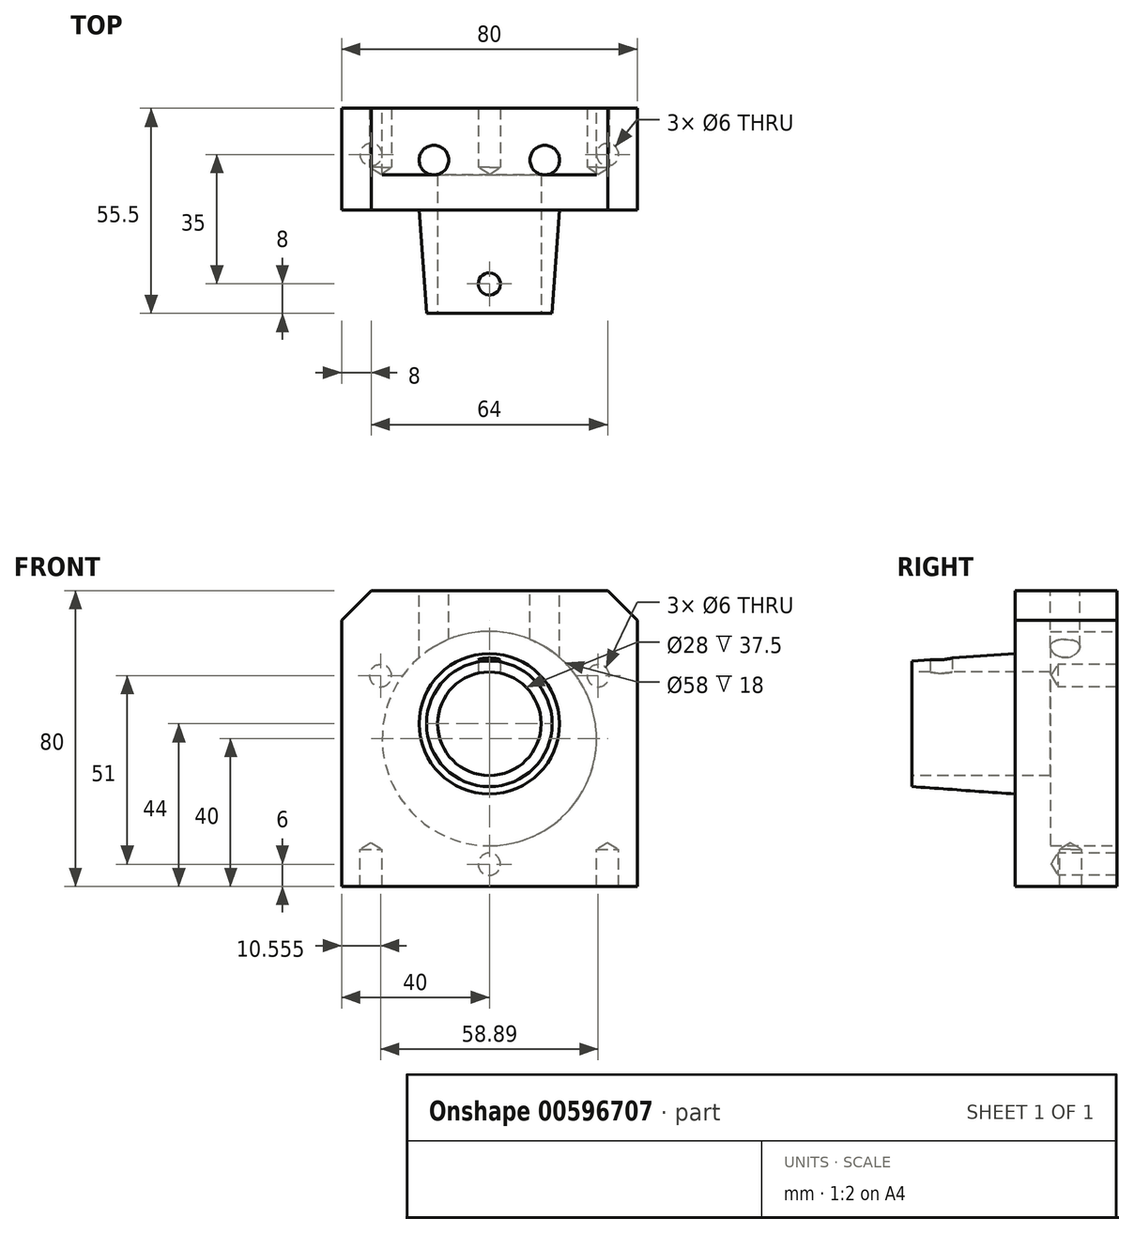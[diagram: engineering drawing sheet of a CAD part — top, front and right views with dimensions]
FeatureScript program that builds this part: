
annotation { "Feature Type Name" : "Feature", "Feature Type Description" : "" }
export const myFeature = defineFeature(function(context is Context, id is Id, definition is map)
    precondition{}
    {
        {
            var Q0;
            Q0=qCreatedBy(makeId("Front.planeOp"),FACE);
            var sketch = newSketch(context, id + "F0", { "sketchPlane" : qUnion([Q0])});
            skLineSegment(sketch, "E0.bottom", {"start": v(-40, 40) * mm, "end": v(40, 40) * mm});
            skLineSegment(sketch, "E0.top", {"start": v(-40, -40) * mm, "end": v(40, -40) * mm});
            skLineSegment(sketch, "E0.left", {"start": v(-40, 40) * mm, "end": v(-40, -40) * mm});
            skLineSegment(sketch, "E0.right", {"start": v(40, 40) * mm, "end": v(40, -40) * mm});
            skCircle(sketch, "E1", {"center": v(0, 0) * mm, "radius": 29 * mm});
            skCircle(sketch, "E2", {"center": v(0, -34) * mm, "radius": 3 * mm});
            skCircle(sketch, "E3.1.0", {"center": v(29.44, 17) * mm, "radius": 3 * mm});
            skCircle(sketch, "E3.2.0", {"center": v(-29.44, 17) * mm, "radius": 3 * mm});
            skSolve(sketch);
        }
        {
            var Q0;
            Q0 = qSketchRegion(id + "F0", true);
            var Q1;
            Q1=makeQuery(id+"F0.imprint","IMPRINT",FACE,{"disambiguationData":[TD([[makeQuery(id+"F0.imprint","IMPRINT",EDGE,{"derivedFrom":sQuery(id+"F0.wireOp",EDGE,"E3.1.0")}),1.0]])]});
            var Q2;
            Q2=makeQuery(id+"F0.imprint","IMPRINT",FACE,{"disambiguationData":[TD([[makeQuery(id+"F0.imprint","IMPRINT",EDGE,{"derivedFrom":sQuery(id+"F0.wireOp",EDGE,"E3.2.0")}),1.0]])]});
            var Q3;
            Q3=makeQuery(id+"F0.imprint","IMPRINT",FACE,{"disambiguationData":[TD([[makeQuery(id+"F0.imprint","IMPRINT",EDGE,{"derivedFrom":sQuery(id+"F0.wireOp",EDGE,"E2")}),1.0]])]});
            var Q4;
            Q4=makeQuery(id+"F0.imprint","IMPRINT",FACE,{"disambiguationData":[TD([[makeQuery(id+"F0.imprint","IMPRINT",EDGE,{"derivedFrom":sQuery(id+"F0.wireOp",EDGE,"E1")}),1.0]])]});
            extrude(context, id + "F1", {"entities" : qUnion([Q0, Q1, Q2, Q3, Q4]), "depth" : 27.5 * mm, "offsetDistance" : 25 * mm});
        }
        {
            var Q0;
            Q0=makeQuery(id+"F1.opExtrude","SWEPT_EDGE",EDGE,{"disambiguationData":[OSD([sQuery(id+"F0.wireOp",EDGE,"E0.bottom"),sQuery(id+"F0.wireOp",EDGE,"E0.right")])]});
            var Q1;
            Q1=makeQuery(id+"F1.opExtrude","SWEPT_EDGE",EDGE,{"disambiguationData":[OSD([sQuery(id+"F0.wireOp",EDGE,"E0.bottom"),sQuery(id+"F0.wireOp",EDGE,"E0.left")])]});
            chamfer(context, id + "F2", {"entities" : qUnion([Q0, Q1]), "width" : 8 * mm, "tangentPropagation" : true});
        }
        {
            var Q0;
            Q0=makeQuery(id+"F1.opExtrude","CAP_FACE",FACE,{"disambiguationData":[OSD([sQuery(id+"F0.wireOp",EDGE,"E0.bottom"),sQuery(id+"F0.wireOp",EDGE,"E0.top"),sQuery(id+"F0.wireOp",EDGE,"E0.left"),sQuery(id+"F0.wireOp",EDGE,"E0.right")])],"isStart":false});
            cPlane(context, id + "F3", {"entities" : qUnion([Q0]), "cplaneType" : CPlaneType.OFFSET, "offset" : 0 * mm, "width" : 150 * mm, "height" : 150 * mm});
        }
        {
            var Q0;
            Q0=qCreatedBy(id+"F3.planeOp",FACE);
            var sketch = newSketch(context, id + "F4", { "sketchPlane" : qUnion([Q0])});
            skPoint(sketch, "E4", {"position": v(0, 4) * mm});
            skSolve(sketch);
        }
        {
            var Q0;
            Q0=qCreatedBy(makeId("Top.planeOp"),FACE);
            var Q1;
            Q1=sQuery(id+"F4.wireOp",VERTEX,"E4");
            cPlane(context, id + "F5", {"entities" : qUnion([Q0, Q1]), "cplaneType" : CPlaneType.PLANE_POINT, "offset" : 25 * mm, "width" : 150 * mm, "height" : 150 * mm});
        }
        {
            var Q0;
            Q0=qCreatedBy(id+"F5.planeOp",FACE);
            var sketch = newSketch(context, id + "F6", { "sketchPlane" : qUnion([Q0])});
            skLineSegment(sketch, "E5", {"start": v(0, -27.5) * mm, "end": v(0, 45.36) * mm, "construction": true});
            skLineSegment(sketch, "E6", {"start": v(0, -27.5) * mm, "end": v(19, -27.5) * mm});
            skLineSegment(sketch, "E7", {"start": v(19, -27.5) * mm, "end": v(17, -55.5) * mm});
            skLineSegment(sketch, "E8", {"start": v(17, -55.5) * mm, "end": v(0, -55.5) * mm});
            skLineSegment(sketch, "E9", {"start": v(0, -55.5) * mm, "end": v(0, -27.5) * mm});
            skSolve(sketch);
        }
        {
            var Q0;
            Q0=qCreatedBy(id+"F5.planeOp",FACE);
            var sketch = newSketch(context, id + "F7", { "sketchPlane" : qUnion([Q0])});
            skLineSegment(sketch, "E10", {"start": v(0, -27.5) * mm, "end": v(19, -27.5) * mm});
            skLineSegment(sketch, "E11", {"start": v(19, -27.5) * mm, "end": v(17, -55.5) * mm});
            skLineSegment(sketch, "E12", {"start": v(17, -55.5) * mm, "end": v(0, -55.5) * mm});
            skLineSegment(sketch, "E13", {"start": v(0, -55.5) * mm, "end": v(0, -27.5) * mm});
            skSolve(sketch);
        }
        {
            var Q0;
            Q0 = qSketchRegion(id + "F7", true);
            var Q1;
            Q1=sQuery(id+"F7.wireOp",EDGE,"E13");
            revolve(context, id + "F8", {"operationType" : NewBodyOperationType.ADD, "entities" : qUnion([Q0]), "axis" : qUnion([Q1]), "revolveType" : RevolveType.FULL});
        }
        {
            var Q0;
            Q0=makeQuery(id+"F8.opRevolve","SWEPT_FACE",FACE,{"disambiguationData":[OSD([sQuery(id+"F7.wireOp",EDGE,"E12")])]});
            var sketch = newSketch(context, id + "F9", { "sketchPlane" : qUnion([Q0])});
            skCircle(sketch, "E14", {"center": v(0, 4) * mm, "radius": 14 * mm});
            skSolve(sketch);
        }
        {
            var Q0;
            Q0 = qSketchRegion(id + "F9", true);
            extrude(context, id + "F10", {"entities" : qUnion([Q0]), "operationType" : NewBodyOperationType.REMOVE, "endBound" : BoundingType.THROUGH_ALL, "oppositeDirection" : true, "depth" : 25 * mm, "offsetDistance" : 25 * mm});
        }
        {
            var Q0;
            Q0=makeQuery(id+"F0.imprint","IMPRINT",FACE,{"disambiguationData":[TD([[makeQuery(id+"F0.imprint","IMPRINT",EDGE,{"derivedFrom":sQuery(id+"F0.wireOp",EDGE,"E1")}),1.0]])]});
            extrude(context, id + "F11", {"entities" : qUnion([Q0]), "operationType" : NewBodyOperationType.REMOVE, "depth" : 18 * mm, "offsetDistance" : 25 * mm});
        }
        {
            var Q0;
            Q0=sQuery(id+"F0.wireOp",VERTEX,"E3.2.0.center");
            var Q1;
            Q1=sQuery(id+"F0.wireOp",VERTEX,"E2.center");
            var Q2;
            Q2=sQuery(id+"F0.wireOp",VERTEX,"E3.1.0.center");
            var Q3;
            Q3=makeQuery(id+"F1.opExtrude","SWEPT_BODY",BODY,{"disambiguationData":[OSD([sQuery(id+"F0.wireOp",EDGE,"E0.bottom"),sQuery(id+"F0.wireOp",EDGE,"E0.top"),sQuery(id+"F0.wireOp",EDGE,"E0.left"),sQuery(id+"F0.wireOp",EDGE,"E0.right")])]});
            hole(context, id + "F12", {"style" : HoleStyle.SIMPLE, "endStyle" : HoleEndStyle.BLIND, "oppositeDirection" : true, "holeDiameter" : 6 * mm, "majorDiameter" : 5 * mm, "holeDepth" : 16 * mm, "isTappedThrough" : true, "tappedDepth" : 12 * mm, "tapClearance" : 3, "startFromSketch" : true, "locations" : qUnion([Q0, Q1, Q2]), "scope" : qUnion([Q3])});
        }
        {
            var Q0;
            Q0=qCreatedBy(id+"F5.planeOp",FACE);
            var sketch = newSketch(context, id + "F13", { "sketchPlane" : qUnion([Q0])});
            skCircle(sketch, "E15", {"center": v(0, -47.5) * mm, "radius": 3 * mm});
            skSolve(sketch);
        }
        {
            var Q0;
            Q0 = qSketchRegion(id + "F13", true);
            extrude(context, id + "F14", {"entities" : qUnion([Q0]), "operationType" : NewBodyOperationType.REMOVE, "depth" : 37 * mm, "offsetDistance" : 25 * mm});
        }
        {
            var Q0;
            Q0=makeQuery(id+"F1.opExtrude","SWEPT_FACE",FACE,{"disambiguationData":[OSD([sQuery(id+"F0.wireOp",EDGE,"E0.bottom")])]});
            var sketch = newSketch(context, id + "F15", { "sketchPlane" : qUnion([Q0])});
            skCircle(sketch, "E16", {"center": v(-15, -14) * mm, "radius": 4 * mm});
            skCircle(sketch, "E17", {"center": v(15, -14) * mm, "radius": 4 * mm});
            skSolve(sketch);
        }
        {
            var Q0;
            Q0 = qSketchRegion(id + "F15", true);
            extrude(context, id + "F16", {"entities" : qUnion([Q0]), "operationType" : NewBodyOperationType.REMOVE, "oppositeDirection" : true, "depth" : 25 * mm, "offsetDistance" : 25 * mm});
        }
        {
            var Q0;
            Q0=makeQuery(id+"F1.opExtrude","SWEPT_FACE",FACE,{"disambiguationData":[OSD([sQuery(id+"F0.wireOp",EDGE,"E0.top")])]});
            var sketch = newSketch(context, id + "F17", { "sketchPlane" : qUnion([Q0])});
            skCircle(sketch, "E18", {"center": v(-32, 12.5) * mm, "radius": 2.5 * mm});
            skCircle(sketch, "E19", {"center": v(32, 12.5) * mm, "radius": 2.5 * mm});
            skSolve(sketch);
        }
        {
            var Q0;
            Q0=sQuery(id+"F17.wireOp",VERTEX,"E18.center");
            var Q1;
            Q1=sQuery(id+"F17.wireOp",VERTEX,"E19.center");
            var Q2;
            Q2=makeQuery(id+"F1.opExtrude","SWEPT_BODY",BODY,{"disambiguationData":[OSD([sQuery(id+"F0.wireOp",EDGE,"E0.bottom"),sQuery(id+"F0.wireOp",EDGE,"E0.top"),sQuery(id+"F0.wireOp",EDGE,"E0.left"),sQuery(id+"F0.wireOp",EDGE,"E0.right")])]});
            hole(context, id + "F18", {"style" : HoleStyle.SIMPLE, "endStyle" : HoleEndStyle.BLIND, "holeDiameter" : 6 * mm, "majorDiameter" : 5 * mm, "holeDepth" : 10 * mm, "isTappedThrough" : true, "tappedDepth" : 12 * mm, "tapClearance" : 3, "startFromSketch" : true, "locations" : qUnion([Q0, Q1]), "scope" : qUnion([Q2])});
        }
    });
